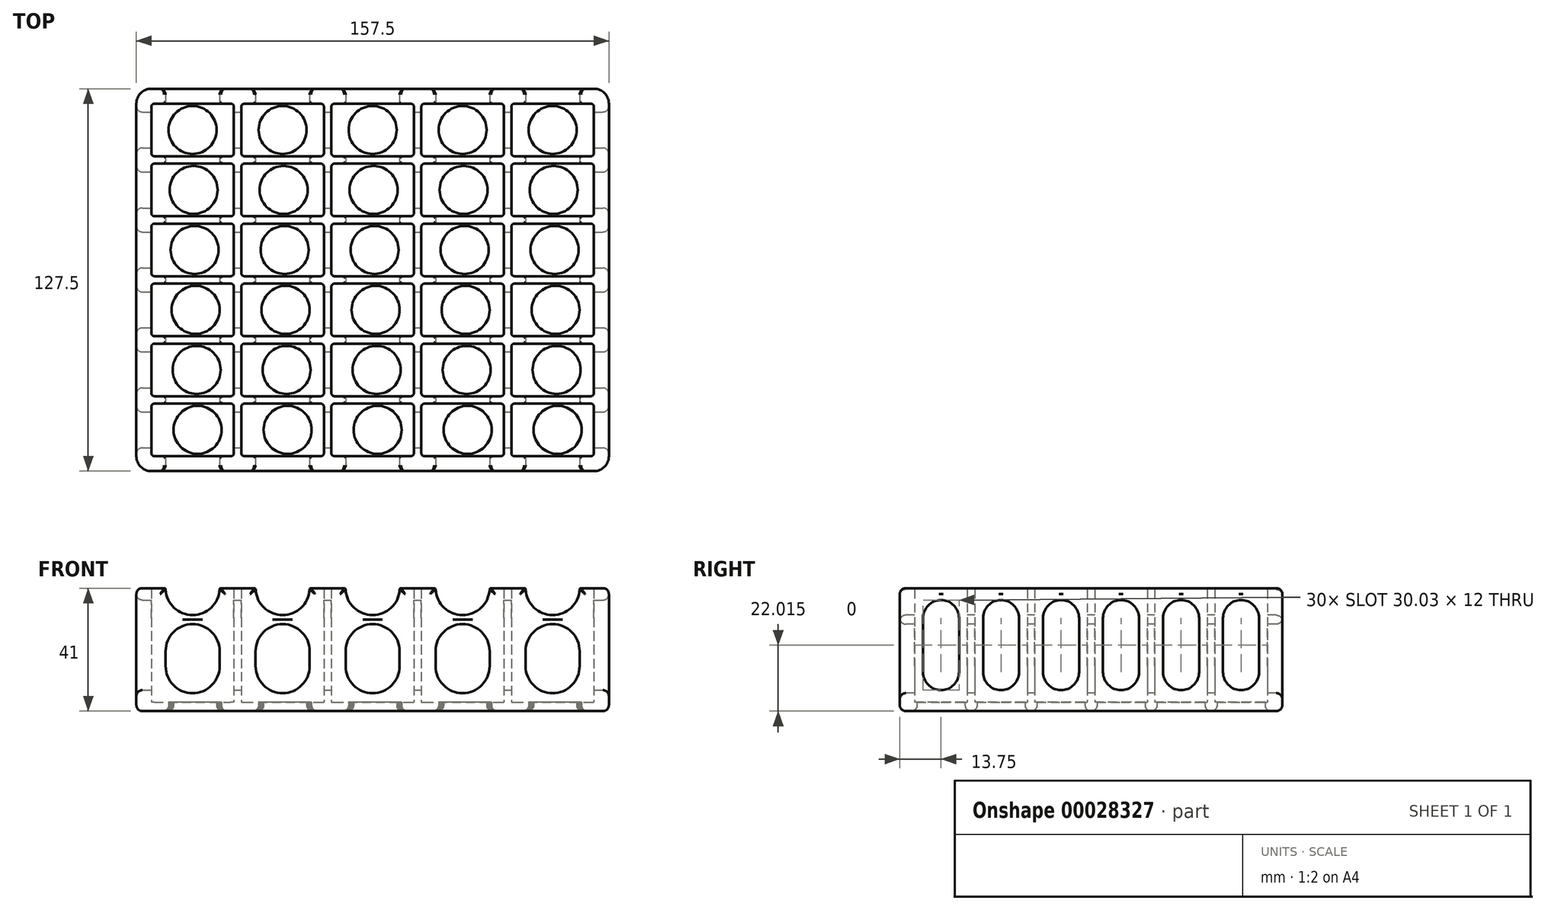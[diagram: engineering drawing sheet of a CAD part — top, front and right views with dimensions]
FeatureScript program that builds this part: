
annotation { "Feature Type Name" : "Feature", "Feature Type Description" : "" }
export const myFeature = defineFeature(function(context is Context, id is Id, definition is map)
    precondition{}
    {
        {
            var Q0;
            Q0=qCreatedBy(makeId("Top.planeOp"),FACE);
            var sketch = newSketch(context, id + "F0", { "sketchPlane" : qUnion([Q0])});
            skLineSegment(sketch, "E0.rect.bottom", {"start": v(73.75, -63.75) * mm, "end": v(-73.75, -63.75) * mm});
            skLineSegment(sketch, "E0.rect.top", {"start": v(73.75, 63.75) * mm, "end": v(-73.75, 63.75) * mm});
            skLineSegment(sketch, "E0.rect.left", {"start": v(78.75, -58.75) * mm, "end": v(78.75, 58.75) * mm});
            skLineSegment(sketch, "E0.rect.right", {"start": v(-78.75, -58.75) * mm, "end": v(-78.75, 58.75) * mm});
            skPoint(sketch, "E0.rect.middle", {"position": v(0, 0) * mm});
            skCircle(sketch, "E1", {"center": v(-60, 50) * mm, "radius": 8 * mm});
            skCircle(sketch, "E2.0.1.0", {"center": v(-59.67, 30) * mm, "radius": 8 * mm});
            skCircle(sketch, "E2.0.2.0", {"center": v(-59.33, 10) * mm, "radius": 8 * mm});
            skCircle(sketch, "E2.0.3.0", {"center": v(-59, -10) * mm, "radius": 8 * mm});
            skCircle(sketch, "E2.0.4.0", {"center": v(-58.67, -29.99) * mm, "radius": 8 * mm});
            skCircle(sketch, "E2.0.5.0", {"center": v(-58.34, -49.99) * mm, "radius": 8 * mm});
            skCircle(sketch, "E2.1.0.0", {"center": v(-30, 50) * mm, "radius": 8 * mm});
            skCircle(sketch, "E2.1.1.0", {"center": v(-29.67, 30) * mm, "radius": 8 * mm});
            skCircle(sketch, "E2.1.2.0", {"center": v(-29.33, 10) * mm, "radius": 8 * mm});
            skCircle(sketch, "E2.1.3.0", {"center": v(-29, -10) * mm, "radius": 8 * mm});
            skCircle(sketch, "E2.1.4.0", {"center": v(-28.67, -29.99) * mm, "radius": 8 * mm});
            skCircle(sketch, "E2.1.5.0", {"center": v(-28.34, -49.99) * mm, "radius": 8 * mm});
            skCircle(sketch, "E2.2.0.0", {"center": v(0, 50) * mm, "radius": 8 * mm});
            skCircle(sketch, "E2.2.1.0", {"center": v(0.33, 30) * mm, "radius": 8 * mm});
            skCircle(sketch, "E2.2.2.0", {"center": v(0.67, 10) * mm, "radius": 8 * mm});
            skCircle(sketch, "E2.2.3.0", {"center": v(1, -10) * mm, "radius": 8 * mm});
            skCircle(sketch, "E2.2.4.0", {"center": v(1.33, -29.99) * mm, "radius": 8 * mm});
            skCircle(sketch, "E2.2.5.0", {"center": v(1.66, -49.99) * mm, "radius": 8 * mm});
            skCircle(sketch, "E2.3.0.0", {"center": v(30, 50) * mm, "radius": 8 * mm});
            skCircle(sketch, "E2.3.1.0", {"center": v(30.33, 30) * mm, "radius": 8 * mm});
            skCircle(sketch, "E2.3.2.0", {"center": v(30.67, 10) * mm, "radius": 8 * mm});
            skCircle(sketch, "E2.3.3.0", {"center": v(31, -10) * mm, "radius": 8 * mm});
            skCircle(sketch, "E2.3.4.0", {"center": v(31.33, -29.99) * mm, "radius": 8 * mm});
            skCircle(sketch, "E2.3.5.0", {"center": v(31.66, -49.99) * mm, "radius": 8 * mm});
            skCircle(sketch, "E2.4.0.0", {"center": v(60, 50) * mm, "radius": 8 * mm});
            skCircle(sketch, "E2.4.1.0", {"center": v(60.33, 30) * mm, "radius": 8 * mm});
            skCircle(sketch, "E2.4.2.0", {"center": v(60.67, 10) * mm, "radius": 8 * mm});
            skCircle(sketch, "E2.4.3.0", {"center": v(61, -10) * mm, "radius": 8 * mm});
            skCircle(sketch, "E2.4.4.0", {"center": v(61.33, -29.99) * mm, "radius": 8 * mm});
            skCircle(sketch, "E2.4.5.0", {"center": v(61.66, -49.99) * mm, "radius": 8 * mm});
            skLineSegment(sketch, "E2.direction1", {"start": v(-60, 50) * mm, "end": v(-30, 50) * mm, "construction": true});
            skLineSegment(sketch, "E2.direction2", {"start": v(-60, 50) * mm, "end": v(-59.67, 30) * mm, "construction": true});
            skPoint(sketch, "E3.visualSharp", {"position": v(78.75, 63.75) * mm});
            skArc(sketch, "E3.filletArc", {"start": v(78.75, 58.75) * mm, "mid": v(77.29, 62.29) * mm, "end": v(73.75, 63.75) * mm});
            skPoint(sketch, "E4.visualSharp", {"position": v(78.75, -63.75) * mm});
            skArc(sketch, "E4.filletArc", {"start": v(73.75, -63.75) * mm, "mid": v(77.29, -62.29) * mm, "end": v(78.75, -58.75) * mm});
            skPoint(sketch, "E5.visualSharp", {"position": v(-78.75, -63.75) * mm});
            skArc(sketch, "E5.filletArc", {"start": v(-78.75, -58.75) * mm, "mid": v(-77.29, -62.29) * mm, "end": v(-73.75, -63.75) * mm});
            skPoint(sketch, "E6.visualSharp", {"position": v(-78.75, 63.75) * mm});
            skArc(sketch, "E6.filletArc", {"start": v(-73.75, 63.75) * mm, "mid": v(-77.29, 62.29) * mm, "end": v(-78.75, 58.75) * mm});
            skSolve(sketch);
        }
        {
            var Q0;
            Q0=qCreatedBy(makeId("Top.planeOp"),FACE);
            var sketch = newSketch(context, id + "F1", { "sketchPlane" : qUnion([Q0])});
            skPoint(sketch, "E7.rect.middle", {"position": v(0, 0) * mm});
            skLineSegment(sketch, "E8.bottom", {"start": v(-72.75, 58.75) * mm, "end": v(-47.25, 58.75) * mm});
            skLineSegment(sketch, "E8.top", {"start": v(-72.75, 41.25) * mm, "end": v(-47.25, 41.25) * mm});
            skLineSegment(sketch, "E8.left", {"start": v(-73.75, 57.75) * mm, "end": v(-73.75, 42.25) * mm});
            skLineSegment(sketch, "E8.right", {"start": v(-46.25, 57.75) * mm, "end": v(-46.25, 42.25) * mm});
            skPoint(sketch, "E9.visualSharp", {"position": v(-46.25, 41.25) * mm});
            skArc(sketch, "E9.filletArc", {"start": v(-47.25, 41.25) * mm, "mid": v(-46.54, 41.54) * mm, "end": v(-46.25, 42.25) * mm});
            skPoint(sketch, "E10.visualSharp", {"position": v(-46.25, 58.75) * mm});
            skArc(sketch, "E10.filletArc", {"start": v(-46.25, 57.75) * mm, "mid": v(-46.54, 58.46) * mm, "end": v(-47.25, 58.75) * mm});
            skPoint(sketch, "E11.visualSharp", {"position": v(-73.75, 58.75) * mm});
            skArc(sketch, "E11.filletArc", {"start": v(-72.75, 58.75) * mm, "mid": v(-73.46, 58.46) * mm, "end": v(-73.75, 57.75) * mm});
            skPoint(sketch, "E12.visualSharp", {"position": v(-73.75, 41.25) * mm});
            skArc(sketch, "E12.filletArc", {"start": v(-73.75, 42.25) * mm, "mid": v(-73.46, 41.54) * mm, "end": v(-72.75, 41.25) * mm});
            skLineSegment(sketch, "E13.0.1.0", {"start": v(-46.25, 37.75) * mm, "end": v(-46.25, 22.25) * mm});
            skLineSegment(sketch, "E13.0.1.1", {"start": v(-72.75, 38.75) * mm, "end": v(-47.25, 38.75) * mm});
            skPoint(sketch, "E13.0.1.2", {"position": v(-73.75, 21.25) * mm});
            skLineSegment(sketch, "E13.0.1.3", {"start": v(-72.75, 21.25) * mm, "end": v(-47.25, 21.25) * mm});
            skPoint(sketch, "E13.0.1.5", {"position": v(-46.25, 21.25) * mm});
            skLineSegment(sketch, "E13.0.1.6", {"start": v(-73.75, 37.75) * mm, "end": v(-73.75, 22.25) * mm});
            skPoint(sketch, "E13.0.1.7", {"position": v(-46.25, 38.75) * mm});
            skPoint(sketch, "E13.0.1.8", {"position": v(-73.75, 38.75) * mm});
            skPoint(sketch, "E13.0.1.10", {"position": v(-78.75, 43.75) * mm});
            skArc(sketch, "E13.0.1.11", {"start": v(-73.75, 22.25) * mm, "mid": v(-73.46, 21.54) * mm, "end": v(-72.75, 21.25) * mm});
            skArc(sketch, "E13.0.1.12", {"start": v(-47.25, 21.25) * mm, "mid": v(-46.54, 21.54) * mm, "end": v(-46.25, 22.25) * mm});
            skArc(sketch, "E13.0.1.13", {"start": v(-72.75, 38.75) * mm, "mid": v(-73.46, 38.46) * mm, "end": v(-73.75, 37.75) * mm});
            skArc(sketch, "E13.0.1.14", {"start": v(-46.25, 37.75) * mm, "mid": v(-46.54, 38.46) * mm, "end": v(-47.25, 38.75) * mm});
            skLineSegment(sketch, "E13.0.2.0", {"start": v(-46.25, 17.75) * mm, "end": v(-46.25, 2.25) * mm});
            skLineSegment(sketch, "E13.0.2.1", {"start": v(-72.75, 18.75) * mm, "end": v(-47.25, 18.75) * mm});
            skPoint(sketch, "E13.0.2.2", {"position": v(-73.75, 1.25) * mm});
            skLineSegment(sketch, "E13.0.2.3", {"start": v(-72.75, 1.25) * mm, "end": v(-47.25, 1.25) * mm});
            skLineSegment(sketch, "E13.0.2.6", {"start": v(-73.75, 17.75) * mm, "end": v(-73.75, 2.25) * mm});
            skPoint(sketch, "E13.0.2.7", {"position": v(-46.25, 18.75) * mm});
            skPoint(sketch, "E13.0.2.8", {"position": v(-73.75, 18.75) * mm});
            skPoint(sketch, "E13.0.2.10", {"position": v(-78.75, 23.75) * mm});
            skArc(sketch, "E13.0.2.11", {"start": v(-73.75, 2.25) * mm, "mid": v(-73.46, 1.54) * mm, "end": v(-72.75, 1.25) * mm});
            skArc(sketch, "E13.0.2.12", {"start": v(-47.25, 1.25) * mm, "mid": v(-46.54, 1.54) * mm, "end": v(-46.25, 2.25) * mm});
            skArc(sketch, "E13.0.2.13", {"start": v(-72.75, 18.75) * mm, "mid": v(-73.46, 18.46) * mm, "end": v(-73.75, 17.75) * mm});
            skArc(sketch, "E13.0.2.14", {"start": v(-46.25, 17.75) * mm, "mid": v(-46.54, 18.46) * mm, "end": v(-47.25, 18.75) * mm});
            skLineSegment(sketch, "E13.0.3.0", {"start": v(-46.25, -2.25) * mm, "end": v(-46.25, -17.75) * mm});
            skLineSegment(sketch, "E13.0.3.1", {"start": v(-72.75, -1.25) * mm, "end": v(-47.25, -1.25) * mm});
            skPoint(sketch, "E13.0.3.2", {"position": v(-73.75, -18.75) * mm});
            skLineSegment(sketch, "E13.0.3.3", {"start": v(-72.75, -18.75) * mm, "end": v(-47.25, -18.75) * mm});
            skPoint(sketch, "E13.0.3.5", {"position": v(-46.25, -18.75) * mm});
            skLineSegment(sketch, "E13.0.3.6", {"start": v(-73.75, -2.25) * mm, "end": v(-73.75, -17.75) * mm});
            skPoint(sketch, "E13.0.3.7", {"position": v(-46.25, -1.25) * mm});
            skPoint(sketch, "E13.0.3.8", {"position": v(-73.75, -1.25) * mm});
            skPoint(sketch, "E13.0.3.10", {"position": v(-78.75, 3.75) * mm});
            skArc(sketch, "E13.0.3.11", {"start": v(-73.75, -17.75) * mm, "mid": v(-73.46, -18.46) * mm, "end": v(-72.75, -18.75) * mm});
            skArc(sketch, "E13.0.3.12", {"start": v(-47.25, -18.75) * mm, "mid": v(-46.54, -18.46) * mm, "end": v(-46.25, -17.75) * mm});
            skArc(sketch, "E13.0.3.13", {"start": v(-72.75, -1.25) * mm, "mid": v(-73.46, -1.54) * mm, "end": v(-73.75, -2.25) * mm});
            skArc(sketch, "E13.0.3.14", {"start": v(-46.25, -2.25) * mm, "mid": v(-46.54, -1.54) * mm, "end": v(-47.25, -1.25) * mm});
            skLineSegment(sketch, "E13.0.4.0", {"start": v(-46.25, -22.25) * mm, "end": v(-46.25, -37.75) * mm});
            skLineSegment(sketch, "E13.0.4.1", {"start": v(-72.75, -21.25) * mm, "end": v(-47.25, -21.25) * mm});
            skPoint(sketch, "E13.0.4.2", {"position": v(-73.75, -38.75) * mm});
            skLineSegment(sketch, "E13.0.4.3", {"start": v(-72.75, -38.75) * mm, "end": v(-47.25, -38.75) * mm});
            skPoint(sketch, "E13.0.4.5", {"position": v(-46.25, -38.75) * mm});
            skLineSegment(sketch, "E13.0.4.6", {"start": v(-73.75, -22.25) * mm, "end": v(-73.75, -37.75) * mm});
            skPoint(sketch, "E13.0.4.7", {"position": v(-46.25, -21.25) * mm});
            skPoint(sketch, "E13.0.4.8", {"position": v(-73.75, -21.25) * mm});
            skPoint(sketch, "E13.0.4.10", {"position": v(-78.75, -16.25) * mm});
            skArc(sketch, "E13.0.4.11", {"start": v(-73.75, -37.75) * mm, "mid": v(-73.46, -38.46) * mm, "end": v(-72.75, -38.75) * mm});
            skArc(sketch, "E13.0.4.12", {"start": v(-47.25, -38.75) * mm, "mid": v(-46.54, -38.46) * mm, "end": v(-46.25, -37.75) * mm});
            skArc(sketch, "E13.0.4.13", {"start": v(-72.75, -21.25) * mm, "mid": v(-73.46, -21.54) * mm, "end": v(-73.75, -22.25) * mm});
            skArc(sketch, "E13.0.4.14", {"start": v(-46.25, -22.25) * mm, "mid": v(-46.54, -21.54) * mm, "end": v(-47.25, -21.25) * mm});
            skLineSegment(sketch, "E13.0.5.0", {"start": v(-46.25, -42.25) * mm, "end": v(-46.25, -57.75) * mm});
            skLineSegment(sketch, "E13.0.5.1", {"start": v(-72.75, -41.25) * mm, "end": v(-47.25, -41.25) * mm});
            skPoint(sketch, "E13.0.5.2", {"position": v(-73.75, -58.75) * mm});
            skLineSegment(sketch, "E13.0.5.3", {"start": v(-72.75, -58.75) * mm, "end": v(-47.25, -58.75) * mm});
            skPoint(sketch, "E13.0.5.5", {"position": v(-46.25, -58.75) * mm});
            skLineSegment(sketch, "E13.0.5.6", {"start": v(-73.75, -42.25) * mm, "end": v(-73.75, -57.75) * mm});
            skPoint(sketch, "E13.0.5.7", {"position": v(-46.25, -41.25) * mm});
            skPoint(sketch, "E13.0.5.8", {"position": v(-73.75, -41.25) * mm});
            skPoint(sketch, "E13.0.5.10", {"position": v(-78.75, -36.25) * mm});
            skArc(sketch, "E13.0.5.11", {"start": v(-73.75, -57.75) * mm, "mid": v(-73.46, -58.46) * mm, "end": v(-72.75, -58.75) * mm});
            skArc(sketch, "E13.0.5.12", {"start": v(-47.25, -58.75) * mm, "mid": v(-46.54, -58.46) * mm, "end": v(-46.25, -57.75) * mm});
            skArc(sketch, "E13.0.5.13", {"start": v(-72.75, -41.25) * mm, "mid": v(-73.46, -41.54) * mm, "end": v(-73.75, -42.25) * mm});
            skArc(sketch, "E13.0.5.14", {"start": v(-46.25, -42.25) * mm, "mid": v(-46.54, -41.54) * mm, "end": v(-47.25, -41.25) * mm});
            skLineSegment(sketch, "E13.1.0.0", {"start": v(-16.25, 57.75) * mm, "end": v(-16.25, 42.25) * mm});
            skLineSegment(sketch, "E13.1.0.1", {"start": v(-42.75, 58.75) * mm, "end": v(-17.25, 58.75) * mm});
            skPoint(sketch, "E13.1.0.2", {"position": v(-43.75, 41.25) * mm});
            skLineSegment(sketch, "E13.1.0.3", {"start": v(-42.75, 41.25) * mm, "end": v(-17.25, 41.25) * mm});
            skPoint(sketch, "E13.1.0.5", {"position": v(-16.25, 41.25) * mm});
            skLineSegment(sketch, "E13.1.0.6", {"start": v(-43.75, 57.75) * mm, "end": v(-43.75, 42.25) * mm});
            skPoint(sketch, "E13.1.0.7", {"position": v(-16.25, 58.75) * mm});
            skPoint(sketch, "E13.1.0.8", {"position": v(-43.75, 58.75) * mm});
            skPoint(sketch, "E13.1.0.10", {"position": v(-48.75, 63.75) * mm});
            skArc(sketch, "E13.1.0.11", {"start": v(-43.75, 42.25) * mm, "mid": v(-43.46, 41.54) * mm, "end": v(-42.75, 41.25) * mm});
            skArc(sketch, "E13.1.0.12", {"start": v(-17.25, 41.25) * mm, "mid": v(-16.54, 41.54) * mm, "end": v(-16.25, 42.25) * mm});
            skArc(sketch, "E13.1.0.13", {"start": v(-42.75, 58.75) * mm, "mid": v(-43.46, 58.46) * mm, "end": v(-43.75, 57.75) * mm});
            skArc(sketch, "E13.1.0.14", {"start": v(-16.25, 57.75) * mm, "mid": v(-16.54, 58.46) * mm, "end": v(-17.25, 58.75) * mm});
            skLineSegment(sketch, "E13.1.1.0", {"start": v(-16.25, 37.75) * mm, "end": v(-16.25, 22.25) * mm});
            skLineSegment(sketch, "E13.1.1.1", {"start": v(-42.75, 38.75) * mm, "end": v(-17.25, 38.75) * mm});
            skPoint(sketch, "E13.1.1.2", {"position": v(-43.75, 21.25) * mm});
            skLineSegment(sketch, "E13.1.1.3", {"start": v(-42.75, 21.25) * mm, "end": v(-17.25, 21.25) * mm});
            skPoint(sketch, "E13.1.1.5", {"position": v(-16.25, 21.25) * mm});
            skLineSegment(sketch, "E13.1.1.6", {"start": v(-43.75, 37.75) * mm, "end": v(-43.75, 22.25) * mm});
            skPoint(sketch, "E13.1.1.7", {"position": v(-16.25, 38.75) * mm});
            skPoint(sketch, "E13.1.1.8", {"position": v(-43.75, 38.75) * mm});
            skPoint(sketch, "E13.1.1.10", {"position": v(-48.75, 43.75) * mm});
            skArc(sketch, "E13.1.1.11", {"start": v(-43.75, 22.25) * mm, "mid": v(-43.46, 21.54) * mm, "end": v(-42.75, 21.25) * mm});
            skArc(sketch, "E13.1.1.12", {"start": v(-17.25, 21.25) * mm, "mid": v(-16.54, 21.54) * mm, "end": v(-16.25, 22.25) * mm});
            skArc(sketch, "E13.1.1.13", {"start": v(-42.75, 38.75) * mm, "mid": v(-43.46, 38.46) * mm, "end": v(-43.75, 37.75) * mm});
            skArc(sketch, "E13.1.1.14", {"start": v(-16.25, 37.75) * mm, "mid": v(-16.54, 38.46) * mm, "end": v(-17.25, 38.75) * mm});
            skLineSegment(sketch, "E13.1.2.0", {"start": v(-16.25, 17.75) * mm, "end": v(-16.25, 2.25) * mm});
            skLineSegment(sketch, "E13.1.2.1", {"start": v(-42.75, 18.75) * mm, "end": v(-17.25, 18.75) * mm});
            skLineSegment(sketch, "E13.1.2.3", {"start": v(-42.75, 1.25) * mm, "end": v(-17.25, 1.25) * mm});
            skPoint(sketch, "E13.1.2.5", {"position": v(-16.25, 1.25) * mm});
            skLineSegment(sketch, "E13.1.2.6", {"start": v(-43.75, 17.75) * mm, "end": v(-43.75, 2.25) * mm});
            skPoint(sketch, "E13.1.2.7", {"position": v(-16.25, 18.75) * mm});
            skPoint(sketch, "E13.1.2.8", {"position": v(-43.75, 18.75) * mm});
            skPoint(sketch, "E13.1.2.10", {"position": v(-48.75, 23.75) * mm});
            skArc(sketch, "E13.1.2.11", {"start": v(-43.75, 2.25) * mm, "mid": v(-43.46, 1.54) * mm, "end": v(-42.75, 1.25) * mm});
            skArc(sketch, "E13.1.2.12", {"start": v(-17.25, 1.25) * mm, "mid": v(-16.54, 1.54) * mm, "end": v(-16.25, 2.25) * mm});
            skArc(sketch, "E13.1.2.13", {"start": v(-42.75, 18.75) * mm, "mid": v(-43.46, 18.46) * mm, "end": v(-43.75, 17.75) * mm});
            skArc(sketch, "E13.1.2.14", {"start": v(-16.25, 17.75) * mm, "mid": v(-16.54, 18.46) * mm, "end": v(-17.25, 18.75) * mm});
            skLineSegment(sketch, "E13.1.3.0", {"start": v(-16.25, -2.25) * mm, "end": v(-16.25, -17.75) * mm});
            skLineSegment(sketch, "E13.1.3.1", {"start": v(-42.75, -1.25) * mm, "end": v(-17.25, -1.25) * mm});
            skPoint(sketch, "E13.1.3.2", {"position": v(-43.75, -18.75) * mm});
            skLineSegment(sketch, "E13.1.3.3", {"start": v(-42.75, -18.75) * mm, "end": v(-17.25, -18.75) * mm});
            skPoint(sketch, "E13.1.3.5", {"position": v(-16.25, -18.75) * mm});
            skLineSegment(sketch, "E13.1.3.6", {"start": v(-43.75, -2.25) * mm, "end": v(-43.75, -17.75) * mm});
            skPoint(sketch, "E13.1.3.7", {"position": v(-16.25, -1.25) * mm});
            skPoint(sketch, "E13.1.3.8", {"position": v(-43.75, -1.25) * mm});
            skPoint(sketch, "E13.1.3.10", {"position": v(-48.75, 3.75) * mm});
            skArc(sketch, "E13.1.3.11", {"start": v(-43.75, -17.75) * mm, "mid": v(-43.46, -18.46) * mm, "end": v(-42.75, -18.75) * mm});
            skArc(sketch, "E13.1.3.12", {"start": v(-17.25, -18.75) * mm, "mid": v(-16.54, -18.46) * mm, "end": v(-16.25, -17.75) * mm});
            skArc(sketch, "E13.1.3.13", {"start": v(-42.75, -1.25) * mm, "mid": v(-43.46, -1.54) * mm, "end": v(-43.75, -2.25) * mm});
            skArc(sketch, "E13.1.3.14", {"start": v(-16.25, -2.25) * mm, "mid": v(-16.54, -1.54) * mm, "end": v(-17.25, -1.25) * mm});
            skLineSegment(sketch, "E13.1.4.0", {"start": v(-16.25, -22.25) * mm, "end": v(-16.25, -37.75) * mm});
            skLineSegment(sketch, "E13.1.4.1", {"start": v(-42.75, -21.25) * mm, "end": v(-17.25, -21.25) * mm});
            skPoint(sketch, "E13.1.4.2", {"position": v(-43.75, -38.75) * mm});
            skLineSegment(sketch, "E13.1.4.3", {"start": v(-42.75, -38.75) * mm, "end": v(-17.25, -38.75) * mm});
            skPoint(sketch, "E13.1.4.5", {"position": v(-16.25, -38.75) * mm});
            skLineSegment(sketch, "E13.1.4.6", {"start": v(-43.75, -22.25) * mm, "end": v(-43.75, -37.75) * mm});
            skPoint(sketch, "E13.1.4.7", {"position": v(-16.25, -21.25) * mm});
            skPoint(sketch, "E13.1.4.8", {"position": v(-43.75, -21.25) * mm});
            skPoint(sketch, "E13.1.4.10", {"position": v(-48.75, -16.25) * mm});
            skArc(sketch, "E13.1.4.11", {"start": v(-43.75, -37.75) * mm, "mid": v(-43.46, -38.46) * mm, "end": v(-42.75, -38.75) * mm});
            skArc(sketch, "E13.1.4.12", {"start": v(-17.25, -38.75) * mm, "mid": v(-16.54, -38.46) * mm, "end": v(-16.25, -37.75) * mm});
            skArc(sketch, "E13.1.4.13", {"start": v(-42.75, -21.25) * mm, "mid": v(-43.46, -21.54) * mm, "end": v(-43.75, -22.25) * mm});
            skArc(sketch, "E13.1.4.14", {"start": v(-16.25, -22.25) * mm, "mid": v(-16.54, -21.54) * mm, "end": v(-17.25, -21.25) * mm});
            skLineSegment(sketch, "E13.1.5.0", {"start": v(-16.25, -42.25) * mm, "end": v(-16.25, -57.75) * mm});
            skLineSegment(sketch, "E13.1.5.1", {"start": v(-42.75, -41.25) * mm, "end": v(-17.25, -41.25) * mm});
            skLineSegment(sketch, "E13.1.5.3", {"start": v(-42.75, -58.75) * mm, "end": v(-17.25, -58.75) * mm});
            skPoint(sketch, "E13.1.5.5", {"position": v(-16.25, -58.75) * mm});
            skLineSegment(sketch, "E13.1.5.6", {"start": v(-43.75, -42.25) * mm, "end": v(-43.75, -57.75) * mm});
            skPoint(sketch, "E13.1.5.7", {"position": v(-16.25, -41.25) * mm});
            skPoint(sketch, "E13.1.5.8", {"position": v(-43.75, -41.25) * mm});
            skPoint(sketch, "E13.1.5.10", {"position": v(-48.75, -36.25) * mm});
            skArc(sketch, "E13.1.5.11", {"start": v(-43.75, -57.75) * mm, "mid": v(-43.46, -58.46) * mm, "end": v(-42.75, -58.75) * mm});
            skArc(sketch, "E13.1.5.12", {"start": v(-17.25, -58.75) * mm, "mid": v(-16.54, -58.46) * mm, "end": v(-16.25, -57.75) * mm});
            skArc(sketch, "E13.1.5.13", {"start": v(-42.75, -41.25) * mm, "mid": v(-43.46, -41.54) * mm, "end": v(-43.75, -42.25) * mm});
            skArc(sketch, "E13.1.5.14", {"start": v(-16.25, -42.25) * mm, "mid": v(-16.54, -41.54) * mm, "end": v(-17.25, -41.25) * mm});
            skLineSegment(sketch, "E13.2.0.0", {"start": v(13.75, 57.75) * mm, "end": v(13.75, 42.25) * mm});
            skLineSegment(sketch, "E13.2.0.1", {"start": v(-12.75, 58.75) * mm, "end": v(12.75, 58.75) * mm});
            skLineSegment(sketch, "E13.2.0.3", {"start": v(-12.75, 41.25) * mm, "end": v(12.75, 41.25) * mm});
            skPoint(sketch, "E13.2.0.5", {"position": v(13.75, 41.25) * mm});
            skLineSegment(sketch, "E13.2.0.6", {"start": v(-13.75, 57.75) * mm, "end": v(-13.75, 42.25) * mm});
            skPoint(sketch, "E13.2.0.7", {"position": v(13.75, 58.75) * mm});
            skPoint(sketch, "E13.2.0.8", {"position": v(-13.75, 58.75) * mm});
            skPoint(sketch, "E13.2.0.10", {"position": v(-18.75, 63.75) * mm});
            skArc(sketch, "E13.2.0.11", {"start": v(-13.75, 42.25) * mm, "mid": v(-13.46, 41.54) * mm, "end": v(-12.75, 41.25) * mm});
            skArc(sketch, "E13.2.0.12", {"start": v(12.75, 41.25) * mm, "mid": v(13.46, 41.54) * mm, "end": v(13.75, 42.25) * mm});
            skArc(sketch, "E13.2.0.13", {"start": v(-12.75, 58.75) * mm, "mid": v(-13.46, 58.46) * mm, "end": v(-13.75, 57.75) * mm});
            skArc(sketch, "E13.2.0.14", {"start": v(13.75, 57.75) * mm, "mid": v(13.46, 58.46) * mm, "end": v(12.75, 58.75) * mm});
            skLineSegment(sketch, "E13.2.1.0", {"start": v(13.75, 37.75) * mm, "end": v(13.75, 22.25) * mm});
            skLineSegment(sketch, "E13.2.1.1", {"start": v(-12.75, 38.75) * mm, "end": v(12.75, 38.75) * mm});
            skPoint(sketch, "E13.2.1.2", {"position": v(-13.75, 21.25) * mm});
            skLineSegment(sketch, "E13.2.1.3", {"start": v(-12.75, 21.25) * mm, "end": v(12.75, 21.25) * mm});
            skPoint(sketch, "E13.2.1.5", {"position": v(13.75, 21.25) * mm});
            skLineSegment(sketch, "E13.2.1.6", {"start": v(-13.75, 37.75) * mm, "end": v(-13.75, 22.25) * mm});
            skPoint(sketch, "E13.2.1.7", {"position": v(13.75, 38.75) * mm});
            skPoint(sketch, "E13.2.1.8", {"position": v(-13.75, 38.75) * mm});
            skPoint(sketch, "E13.2.1.10", {"position": v(-18.75, 43.75) * mm});
            skArc(sketch, "E13.2.1.11", {"start": v(-13.75, 22.25) * mm, "mid": v(-13.46, 21.54) * mm, "end": v(-12.75, 21.25) * mm});
            skArc(sketch, "E13.2.1.12", {"start": v(12.75, 21.25) * mm, "mid": v(13.46, 21.54) * mm, "end": v(13.75, 22.25) * mm});
            skArc(sketch, "E13.2.1.13", {"start": v(-12.75, 38.75) * mm, "mid": v(-13.46, 38.46) * mm, "end": v(-13.75, 37.75) * mm});
            skArc(sketch, "E13.2.1.14", {"start": v(13.75, 37.75) * mm, "mid": v(13.46, 38.46) * mm, "end": v(12.75, 38.75) * mm});
            skLineSegment(sketch, "E13.2.2.0", {"start": v(13.75, 17.75) * mm, "end": v(13.75, 2.25) * mm});
            skLineSegment(sketch, "E13.2.2.1", {"start": v(-12.75, 18.75) * mm, "end": v(12.75, 18.75) * mm});
            skPoint(sketch, "E13.2.2.2", {"position": v(-13.75, 1.25) * mm});
            skLineSegment(sketch, "E13.2.2.3", {"start": v(-12.75, 1.25) * mm, "end": v(12.75, 1.25) * mm});
            skPoint(sketch, "E13.2.2.5", {"position": v(13.75, 1.25) * mm});
            skLineSegment(sketch, "E13.2.2.6", {"start": v(-13.75, 17.75) * mm, "end": v(-13.75, 2.25) * mm});
            skPoint(sketch, "E13.2.2.7", {"position": v(13.75, 18.75) * mm});
            skPoint(sketch, "E13.2.2.8", {"position": v(-13.75, 18.75) * mm});
            skPoint(sketch, "E13.2.2.10", {"position": v(-18.75, 23.75) * mm});
            skArc(sketch, "E13.2.2.11", {"start": v(-13.75, 2.25) * mm, "mid": v(-13.46, 1.54) * mm, "end": v(-12.75, 1.25) * mm});
            skArc(sketch, "E13.2.2.12", {"start": v(12.75, 1.25) * mm, "mid": v(13.46, 1.54) * mm, "end": v(13.75, 2.25) * mm});
            skArc(sketch, "E13.2.2.13", {"start": v(-12.75, 18.75) * mm, "mid": v(-13.46, 18.46) * mm, "end": v(-13.75, 17.75) * mm});
            skArc(sketch, "E13.2.2.14", {"start": v(13.75, 17.75) * mm, "mid": v(13.46, 18.46) * mm, "end": v(12.75, 18.75) * mm});
            skLineSegment(sketch, "E13.2.3.0", {"start": v(13.75, -2.25) * mm, "end": v(13.75, -17.75) * mm});
            skLineSegment(sketch, "E13.2.3.1", {"start": v(-12.75, -1.25) * mm, "end": v(12.75, -1.25) * mm});
            skPoint(sketch, "E13.2.3.2", {"position": v(-13.75, -18.75) * mm});
            skLineSegment(sketch, "E13.2.3.3", {"start": v(-12.75, -18.75) * mm, "end": v(12.75, -18.75) * mm});
            skPoint(sketch, "E13.2.3.5", {"position": v(13.75, -18.75) * mm});
            skLineSegment(sketch, "E13.2.3.6", {"start": v(-13.75, -2.25) * mm, "end": v(-13.75, -17.75) * mm});
            skPoint(sketch, "E13.2.3.7", {"position": v(13.75, -1.25) * mm});
            skPoint(sketch, "E13.2.3.8", {"position": v(-13.75, -1.25) * mm});
            skPoint(sketch, "E13.2.3.10", {"position": v(-18.75, 3.75) * mm});
            skArc(sketch, "E13.2.3.11", {"start": v(-13.75, -17.75) * mm, "mid": v(-13.46, -18.46) * mm, "end": v(-12.75, -18.75) * mm});
            skArc(sketch, "E13.2.3.12", {"start": v(12.75, -18.75) * mm, "mid": v(13.46, -18.46) * mm, "end": v(13.75, -17.75) * mm});
            skArc(sketch, "E13.2.3.13", {"start": v(-12.75, -1.25) * mm, "mid": v(-13.46, -1.54) * mm, "end": v(-13.75, -2.25) * mm});
            skArc(sketch, "E13.2.3.14", {"start": v(13.75, -2.25) * mm, "mid": v(13.46, -1.54) * mm, "end": v(12.75, -1.25) * mm});
            skLineSegment(sketch, "E13.2.4.0", {"start": v(13.75, -22.25) * mm, "end": v(13.75, -37.75) * mm});
            skLineSegment(sketch, "E13.2.4.1", {"start": v(-12.75, -21.25) * mm, "end": v(12.75, -21.25) * mm});
            skPoint(sketch, "E13.2.4.2", {"position": v(-13.75, -38.75) * mm});
            skLineSegment(sketch, "E13.2.4.3", {"start": v(-12.75, -38.75) * mm, "end": v(12.75, -38.75) * mm});
            skPoint(sketch, "E13.2.4.5", {"position": v(13.75, -38.75) * mm});
            skLineSegment(sketch, "E13.2.4.6", {"start": v(-13.75, -22.25) * mm, "end": v(-13.75, -37.75) * mm});
            skPoint(sketch, "E13.2.4.7", {"position": v(13.75, -21.25) * mm});
            skPoint(sketch, "E13.2.4.8", {"position": v(-13.75, -21.25) * mm});
            skPoint(sketch, "E13.2.4.10", {"position": v(-18.75, -16.25) * mm});
            skArc(sketch, "E13.2.4.11", {"start": v(-13.75, -37.75) * mm, "mid": v(-13.46, -38.46) * mm, "end": v(-12.75, -38.75) * mm});
            skArc(sketch, "E13.2.4.12", {"start": v(12.75, -38.75) * mm, "mid": v(13.46, -38.46) * mm, "end": v(13.75, -37.75) * mm});
            skArc(sketch, "E13.2.4.13", {"start": v(-12.75, -21.25) * mm, "mid": v(-13.46, -21.54) * mm, "end": v(-13.75, -22.25) * mm});
            skArc(sketch, "E13.2.4.14", {"start": v(13.75, -22.25) * mm, "mid": v(13.46, -21.54) * mm, "end": v(12.75, -21.25) * mm});
            skLineSegment(sketch, "E13.2.5.0", {"start": v(13.75, -42.25) * mm, "end": v(13.75, -57.75) * mm});
            skLineSegment(sketch, "E13.2.5.1", {"start": v(-12.75, -41.25) * mm, "end": v(12.75, -41.25) * mm});
            skLineSegment(sketch, "E13.2.5.3", {"start": v(-12.75, -58.75) * mm, "end": v(12.75, -58.75) * mm});
            skPoint(sketch, "E13.2.5.5", {"position": v(13.75, -58.75) * mm});
            skLineSegment(sketch, "E13.2.5.6", {"start": v(-13.75, -42.25) * mm, "end": v(-13.75, -57.75) * mm});
            skPoint(sketch, "E13.2.5.7", {"position": v(13.75, -41.25) * mm});
            skPoint(sketch, "E13.2.5.8", {"position": v(-13.75, -41.25) * mm});
            skPoint(sketch, "E13.2.5.10", {"position": v(-18.75, -36.25) * mm});
            skArc(sketch, "E13.2.5.11", {"start": v(-13.75, -57.75) * mm, "mid": v(-13.46, -58.46) * mm, "end": v(-12.75, -58.75) * mm});
            skArc(sketch, "E13.2.5.12", {"start": v(12.75, -58.75) * mm, "mid": v(13.46, -58.46) * mm, "end": v(13.75, -57.75) * mm});
            skArc(sketch, "E13.2.5.13", {"start": v(-12.75, -41.25) * mm, "mid": v(-13.46, -41.54) * mm, "end": v(-13.75, -42.25) * mm});
            skArc(sketch, "E13.2.5.14", {"start": v(13.75, -42.25) * mm, "mid": v(13.46, -41.54) * mm, "end": v(12.75, -41.25) * mm});
            skLineSegment(sketch, "E13.3.0.0", {"start": v(43.75, 57.75) * mm, "end": v(43.75, 42.25) * mm});
            skLineSegment(sketch, "E13.3.0.1", {"start": v(17.25, 58.75) * mm, "end": v(42.75, 58.75) * mm});
            skPoint(sketch, "E13.3.0.2", {"position": v(16.25, 41.25) * mm});
            skLineSegment(sketch, "E13.3.0.3", {"start": v(17.25, 41.25) * mm, "end": v(42.75, 41.25) * mm});
            skPoint(sketch, "E13.3.0.5", {"position": v(43.75, 41.25) * mm});
            skLineSegment(sketch, "E13.3.0.6", {"start": v(16.25, 57.75) * mm, "end": v(16.25, 42.25) * mm});
            skPoint(sketch, "E13.3.0.7", {"position": v(43.75, 58.75) * mm});
            skPoint(sketch, "E13.3.0.8", {"position": v(16.25, 58.75) * mm});
            skPoint(sketch, "E13.3.0.10", {"position": v(11.25, 63.75) * mm});
            skArc(sketch, "E13.3.0.11", {"start": v(16.25, 42.25) * mm, "mid": v(16.54, 41.54) * mm, "end": v(17.25, 41.25) * mm});
            skArc(sketch, "E13.3.0.12", {"start": v(42.75, 41.25) * mm, "mid": v(43.46, 41.54) * mm, "end": v(43.75, 42.25) * mm});
            skArc(sketch, "E13.3.0.13", {"start": v(17.25, 58.75) * mm, "mid": v(16.54, 58.46) * mm, "end": v(16.25, 57.75) * mm});
            skArc(sketch, "E13.3.0.14", {"start": v(43.75, 57.75) * mm, "mid": v(43.46, 58.46) * mm, "end": v(42.75, 58.75) * mm});
            skLineSegment(sketch, "E13.3.1.0", {"start": v(43.75, 37.75) * mm, "end": v(43.75, 22.25) * mm});
            skLineSegment(sketch, "E13.3.1.1", {"start": v(17.25, 38.75) * mm, "end": v(42.75, 38.75) * mm});
            skPoint(sketch, "E13.3.1.2", {"position": v(16.25, 21.25) * mm});
            skLineSegment(sketch, "E13.3.1.3", {"start": v(17.25, 21.25) * mm, "end": v(42.75, 21.25) * mm});
            skPoint(sketch, "E13.3.1.5", {"position": v(43.75, 21.25) * mm});
            skLineSegment(sketch, "E13.3.1.6", {"start": v(16.25, 37.75) * mm, "end": v(16.25, 22.25) * mm});
            skPoint(sketch, "E13.3.1.7", {"position": v(43.75, 38.75) * mm});
            skPoint(sketch, "E13.3.1.8", {"position": v(16.25, 38.75) * mm});
            skPoint(sketch, "E13.3.1.10", {"position": v(11.25, 43.75) * mm});
            skArc(sketch, "E13.3.1.11", {"start": v(16.25, 22.25) * mm, "mid": v(16.54, 21.54) * mm, "end": v(17.25, 21.25) * mm});
            skArc(sketch, "E13.3.1.12", {"start": v(42.75, 21.25) * mm, "mid": v(43.46, 21.54) * mm, "end": v(43.75, 22.25) * mm});
            skArc(sketch, "E13.3.1.13", {"start": v(17.25, 38.75) * mm, "mid": v(16.54, 38.46) * mm, "end": v(16.25, 37.75) * mm});
            skArc(sketch, "E13.3.1.14", {"start": v(43.75, 37.75) * mm, "mid": v(43.46, 38.46) * mm, "end": v(42.75, 38.75) * mm});
            skLineSegment(sketch, "E13.3.2.0", {"start": v(43.75, 17.75) * mm, "end": v(43.75, 2.25) * mm});
            skLineSegment(sketch, "E13.3.2.1", {"start": v(17.25, 18.75) * mm, "end": v(42.75, 18.75) * mm});
            skPoint(sketch, "E13.3.2.2", {"position": v(16.25, 1.25) * mm});
            skLineSegment(sketch, "E13.3.2.3", {"start": v(17.25, 1.25) * mm, "end": v(42.75, 1.25) * mm});
            skPoint(sketch, "E13.3.2.5", {"position": v(43.75, 1.25) * mm});
            skLineSegment(sketch, "E13.3.2.6", {"start": v(16.25, 17.75) * mm, "end": v(16.25, 2.25) * mm});
            skPoint(sketch, "E13.3.2.7", {"position": v(43.75, 18.75) * mm});
            skPoint(sketch, "E13.3.2.8", {"position": v(16.25, 18.75) * mm});
            skPoint(sketch, "E13.3.2.10", {"position": v(11.25, 23.75) * mm});
            skArc(sketch, "E13.3.2.11", {"start": v(16.25, 2.25) * mm, "mid": v(16.54, 1.54) * mm, "end": v(17.25, 1.25) * mm});
            skArc(sketch, "E13.3.2.12", {"start": v(42.75, 1.25) * mm, "mid": v(43.46, 1.54) * mm, "end": v(43.75, 2.25) * mm});
            skArc(sketch, "E13.3.2.13", {"start": v(17.25, 18.75) * mm, "mid": v(16.54, 18.46) * mm, "end": v(16.25, 17.75) * mm});
            skArc(sketch, "E13.3.2.14", {"start": v(43.75, 17.75) * mm, "mid": v(43.46, 18.46) * mm, "end": v(42.75, 18.75) * mm});
            skLineSegment(sketch, "E13.3.3.0", {"start": v(43.75, -2.25) * mm, "end": v(43.75, -17.75) * mm});
            skLineSegment(sketch, "E13.3.3.1", {"start": v(17.25, -1.25) * mm, "end": v(42.75, -1.25) * mm});
            skPoint(sketch, "E13.3.3.2", {"position": v(16.25, -18.75) * mm});
            skLineSegment(sketch, "E13.3.3.3", {"start": v(17.25, -18.75) * mm, "end": v(42.75, -18.75) * mm});
            skLineSegment(sketch, "E13.3.3.6", {"start": v(16.25, -2.25) * mm, "end": v(16.25, -17.75) * mm});
            skPoint(sketch, "E13.3.3.7", {"position": v(43.75, -1.25) * mm});
            skPoint(sketch, "E13.3.3.8", {"position": v(16.25, -1.25) * mm});
            skPoint(sketch, "E13.3.3.10", {"position": v(11.25, 3.75) * mm});
            skArc(sketch, "E13.3.3.11", {"start": v(16.25, -17.75) * mm, "mid": v(16.54, -18.46) * mm, "end": v(17.25, -18.75) * mm});
            skArc(sketch, "E13.3.3.12", {"start": v(42.75, -18.75) * mm, "mid": v(43.46, -18.46) * mm, "end": v(43.75, -17.75) * mm});
            skArc(sketch, "E13.3.3.13", {"start": v(17.25, -1.25) * mm, "mid": v(16.54, -1.54) * mm, "end": v(16.25, -2.25) * mm});
            skArc(sketch, "E13.3.3.14", {"start": v(43.75, -2.25) * mm, "mid": v(43.46, -1.54) * mm, "end": v(42.75, -1.25) * mm});
            skLineSegment(sketch, "E13.3.4.0", {"start": v(43.75, -22.25) * mm, "end": v(43.75, -37.75) * mm});
            skLineSegment(sketch, "E13.3.4.1", {"start": v(17.25, -21.25) * mm, "end": v(42.75, -21.25) * mm});
            skPoint(sketch, "E13.3.4.2", {"position": v(16.25, -38.75) * mm});
            skLineSegment(sketch, "E13.3.4.3", {"start": v(17.25, -38.75) * mm, "end": v(42.75, -38.75) * mm});
            skPoint(sketch, "E13.3.4.5", {"position": v(43.75, -38.75) * mm});
            skLineSegment(sketch, "E13.3.4.6", {"start": v(16.25, -22.25) * mm, "end": v(16.25, -37.75) * mm});
            skPoint(sketch, "E13.3.4.7", {"position": v(43.75, -21.25) * mm});
            skPoint(sketch, "E13.3.4.8", {"position": v(16.25, -21.25) * mm});
            skPoint(sketch, "E13.3.4.10", {"position": v(11.25, -16.25) * mm});
            skArc(sketch, "E13.3.4.11", {"start": v(16.25, -37.75) * mm, "mid": v(16.54, -38.46) * mm, "end": v(17.25, -38.75) * mm});
            skArc(sketch, "E13.3.4.12", {"start": v(42.75, -38.75) * mm, "mid": v(43.46, -38.46) * mm, "end": v(43.75, -37.75) * mm});
            skArc(sketch, "E13.3.4.13", {"start": v(17.25, -21.25) * mm, "mid": v(16.54, -21.54) * mm, "end": v(16.25, -22.25) * mm});
            skArc(sketch, "E13.3.4.14", {"start": v(43.75, -22.25) * mm, "mid": v(43.46, -21.54) * mm, "end": v(42.75, -21.25) * mm});
            skLineSegment(sketch, "E13.3.5.0", {"start": v(43.75, -42.25) * mm, "end": v(43.75, -57.75) * mm});
            skLineSegment(sketch, "E13.3.5.1", {"start": v(17.25, -41.25) * mm, "end": v(42.75, -41.25) * mm});
            skLineSegment(sketch, "E13.3.5.3", {"start": v(17.25, -58.75) * mm, "end": v(42.75, -58.75) * mm});
            skPoint(sketch, "E13.3.5.5", {"position": v(43.75, -58.75) * mm});
            skLineSegment(sketch, "E13.3.5.6", {"start": v(16.25, -42.25) * mm, "end": v(16.25, -57.75) * mm});
            skPoint(sketch, "E13.3.5.7", {"position": v(43.75, -41.25) * mm});
            skPoint(sketch, "E13.3.5.8", {"position": v(16.25, -41.25) * mm});
            skPoint(sketch, "E13.3.5.10", {"position": v(11.25, -36.25) * mm});
            skArc(sketch, "E13.3.5.11", {"start": v(16.25, -57.75) * mm, "mid": v(16.54, -58.46) * mm, "end": v(17.25, -58.75) * mm});
            skArc(sketch, "E13.3.5.12", {"start": v(42.75, -58.75) * mm, "mid": v(43.46, -58.46) * mm, "end": v(43.75, -57.75) * mm});
            skArc(sketch, "E13.3.5.13", {"start": v(17.25, -41.25) * mm, "mid": v(16.54, -41.54) * mm, "end": v(16.25, -42.25) * mm});
            skArc(sketch, "E13.3.5.14", {"start": v(43.75, -42.25) * mm, "mid": v(43.46, -41.54) * mm, "end": v(42.75, -41.25) * mm});
            skLineSegment(sketch, "E13.4.0.0", {"start": v(73.75, 57.75) * mm, "end": v(73.75, 42.25) * mm});
            skLineSegment(sketch, "E13.4.0.1", {"start": v(47.25, 58.75) * mm, "end": v(72.75, 58.75) * mm});
            skLineSegment(sketch, "E13.4.0.3", {"start": v(47.25, 41.25) * mm, "end": v(72.75, 41.25) * mm});
            skPoint(sketch, "E13.4.0.5", {"position": v(73.75, 41.25) * mm});
            skLineSegment(sketch, "E13.4.0.6", {"start": v(46.25, 57.75) * mm, "end": v(46.25, 42.25) * mm});
            skPoint(sketch, "E13.4.0.8", {"position": v(46.25, 58.75) * mm});
            skPoint(sketch, "E13.4.0.10", {"position": v(41.25, 63.75) * mm});
            skArc(sketch, "E13.4.0.11", {"start": v(46.25, 42.25) * mm, "mid": v(46.54, 41.54) * mm, "end": v(47.25, 41.25) * mm});
            skArc(sketch, "E13.4.0.12", {"start": v(72.75, 41.25) * mm, "mid": v(73.46, 41.54) * mm, "end": v(73.75, 42.25) * mm});
            skArc(sketch, "E13.4.0.13", {"start": v(47.25, 58.75) * mm, "mid": v(46.54, 58.46) * mm, "end": v(46.25, 57.75) * mm});
            skLineSegment(sketch, "E13.4.1.0", {"start": v(73.75, 37.75) * mm, "end": v(73.75, 22.25) * mm});
            skLineSegment(sketch, "E13.4.1.1", {"start": v(47.25, 38.75) * mm, "end": v(72.75, 38.75) * mm});
            skPoint(sketch, "E13.4.1.2", {"position": v(46.25, 21.25) * mm});
            skLineSegment(sketch, "E13.4.1.3", {"start": v(47.25, 21.25) * mm, "end": v(72.75, 21.25) * mm});
            skPoint(sketch, "E13.4.1.5", {"position": v(73.75, 21.25) * mm});
            skLineSegment(sketch, "E13.4.1.6", {"start": v(46.25, 37.75) * mm, "end": v(46.25, 22.25) * mm});
            skPoint(sketch, "E13.4.1.7", {"position": v(73.75, 38.75) * mm});
            skPoint(sketch, "E13.4.1.8", {"position": v(46.25, 38.75) * mm});
            skPoint(sketch, "E13.4.1.10", {"position": v(41.25, 43.75) * mm});
            skArc(sketch, "E13.4.1.11", {"start": v(46.25, 22.25) * mm, "mid": v(46.54, 21.54) * mm, "end": v(47.25, 21.25) * mm});
            skArc(sketch, "E13.4.1.12", {"start": v(72.75, 21.25) * mm, "mid": v(73.46, 21.54) * mm, "end": v(73.75, 22.25) * mm});
            skArc(sketch, "E13.4.1.13", {"start": v(47.25, 38.75) * mm, "mid": v(46.54, 38.46) * mm, "end": v(46.25, 37.75) * mm});
            skArc(sketch, "E13.4.1.14", {"start": v(73.75, 37.75) * mm, "mid": v(73.46, 38.46) * mm, "end": v(72.75, 38.75) * mm});
            skLineSegment(sketch, "E13.4.2.0", {"start": v(73.75, 17.75) * mm, "end": v(73.75, 2.25) * mm});
            skLineSegment(sketch, "E13.4.2.1", {"start": v(47.25, 18.75) * mm, "end": v(72.75, 18.75) * mm});
            skPoint(sketch, "E13.4.2.2", {"position": v(46.25, 1.25) * mm});
            skLineSegment(sketch, "E13.4.2.3", {"start": v(47.25, 1.25) * mm, "end": v(72.75, 1.25) * mm});
            skPoint(sketch, "E13.4.2.5", {"position": v(73.75, 1.25) * mm});
            skLineSegment(sketch, "E13.4.2.6", {"start": v(46.25, 17.75) * mm, "end": v(46.25, 2.25) * mm});
            skPoint(sketch, "E13.4.2.7", {"position": v(73.75, 18.75) * mm});
            skPoint(sketch, "E13.4.2.8", {"position": v(46.25, 18.75) * mm});
            skPoint(sketch, "E13.4.2.10", {"position": v(41.25, 23.75) * mm});
            skArc(sketch, "E13.4.2.11", {"start": v(46.25, 2.25) * mm, "mid": v(46.54, 1.54) * mm, "end": v(47.25, 1.25) * mm});
            skArc(sketch, "E13.4.2.12", {"start": v(72.75, 1.25) * mm, "mid": v(73.46, 1.54) * mm, "end": v(73.75, 2.25) * mm});
            skArc(sketch, "E13.4.2.13", {"start": v(47.25, 18.75) * mm, "mid": v(46.54, 18.46) * mm, "end": v(46.25, 17.75) * mm});
            skArc(sketch, "E13.4.2.14", {"start": v(73.75, 17.75) * mm, "mid": v(73.46, 18.46) * mm, "end": v(72.75, 18.75) * mm});
            skLineSegment(sketch, "E13.4.3.0", {"start": v(73.75, -2.25) * mm, "end": v(73.75, -17.75) * mm});
            skLineSegment(sketch, "E13.4.3.1", {"start": v(47.25, -1.25) * mm, "end": v(72.75, -1.25) * mm});
            skPoint(sketch, "E13.4.3.2", {"position": v(46.25, -18.75) * mm});
            skLineSegment(sketch, "E13.4.3.3", {"start": v(47.25, -18.75) * mm, "end": v(72.75, -18.75) * mm});
            skPoint(sketch, "E13.4.3.5", {"position": v(73.75, -18.75) * mm});
            skLineSegment(sketch, "E13.4.3.6", {"start": v(46.25, -2.25) * mm, "end": v(46.25, -17.75) * mm});
            skPoint(sketch, "E13.4.3.7", {"position": v(73.75, -1.25) * mm});
            skPoint(sketch, "E13.4.3.8", {"position": v(46.25, -1.25) * mm});
            skPoint(sketch, "E13.4.3.10", {"position": v(41.25, 3.75) * mm});
            skArc(sketch, "E13.4.3.11", {"start": v(46.25, -17.75) * mm, "mid": v(46.54, -18.46) * mm, "end": v(47.25, -18.75) * mm});
            skArc(sketch, "E13.4.3.12", {"start": v(72.75, -18.75) * mm, "mid": v(73.46, -18.46) * mm, "end": v(73.75, -17.75) * mm});
            skArc(sketch, "E13.4.3.13", {"start": v(47.25, -1.25) * mm, "mid": v(46.54, -1.54) * mm, "end": v(46.25, -2.25) * mm});
            skArc(sketch, "E13.4.3.14", {"start": v(73.75, -2.25) * mm, "mid": v(73.46, -1.54) * mm, "end": v(72.75, -1.25) * mm});
            skLineSegment(sketch, "E13.4.4.0", {"start": v(73.75, -22.25) * mm, "end": v(73.75, -37.75) * mm});
            skLineSegment(sketch, "E13.4.4.1", {"start": v(47.25, -21.25) * mm, "end": v(72.75, -21.25) * mm});
            skPoint(sketch, "E13.4.4.2", {"position": v(46.25, -38.75) * mm});
            skLineSegment(sketch, "E13.4.4.3", {"start": v(47.25, -38.75) * mm, "end": v(72.75, -38.75) * mm});
            skPoint(sketch, "E13.4.4.5", {"position": v(73.75, -38.75) * mm});
            skLineSegment(sketch, "E13.4.4.6", {"start": v(46.25, -22.25) * mm, "end": v(46.25, -37.75) * mm});
            skPoint(sketch, "E13.4.4.7", {"position": v(73.75, -21.25) * mm});
            skPoint(sketch, "E13.4.4.8", {"position": v(46.25, -21.25) * mm});
            skPoint(sketch, "E13.4.4.10", {"position": v(41.25, -16.25) * mm});
            skArc(sketch, "E13.4.4.11", {"start": v(46.25, -37.75) * mm, "mid": v(46.54, -38.46) * mm, "end": v(47.25, -38.75) * mm});
            skArc(sketch, "E13.4.4.12", {"start": v(72.75, -38.75) * mm, "mid": v(73.46, -38.46) * mm, "end": v(73.75, -37.75) * mm});
            skArc(sketch, "E13.4.4.13", {"start": v(47.25, -21.25) * mm, "mid": v(46.54, -21.54) * mm, "end": v(46.25, -22.25) * mm});
            skArc(sketch, "E13.4.4.14", {"start": v(73.75, -22.25) * mm, "mid": v(73.46, -21.54) * mm, "end": v(72.75, -21.25) * mm});
            skLineSegment(sketch, "E13.4.5.0", {"start": v(73.75, -42.25) * mm, "end": v(73.75, -57.75) * mm});
            skLineSegment(sketch, "E13.4.5.1", {"start": v(47.25, -41.25) * mm, "end": v(72.75, -41.25) * mm});
            skLineSegment(sketch, "E13.4.5.3", {"start": v(47.25, -58.75) * mm, "end": v(72.75, -58.75) * mm});
            skPoint(sketch, "E13.4.5.5", {"position": v(73.75, -58.75) * mm});
            skLineSegment(sketch, "E13.4.5.6", {"start": v(46.25, -42.25) * mm, "end": v(46.25, -57.75) * mm});
            skPoint(sketch, "E13.4.5.7", {"position": v(73.75, -41.25) * mm});
            skPoint(sketch, "E13.4.5.8", {"position": v(46.25, -41.25) * mm});
            skPoint(sketch, "E13.4.5.10", {"position": v(41.25, -36.25) * mm});
            skArc(sketch, "E13.4.5.11", {"start": v(46.25, -57.75) * mm, "mid": v(46.54, -58.46) * mm, "end": v(47.25, -58.75) * mm});
            skArc(sketch, "E13.4.5.12", {"start": v(72.75, -58.75) * mm, "mid": v(73.46, -58.46) * mm, "end": v(73.75, -57.75) * mm});
            skArc(sketch, "E13.4.5.13", {"start": v(47.25, -41.25) * mm, "mid": v(46.54, -41.54) * mm, "end": v(46.25, -42.25) * mm});
            skArc(sketch, "E13.4.5.14", {"start": v(73.75, -42.25) * mm, "mid": v(73.46, -41.54) * mm, "end": v(72.75, -41.25) * mm});
            skLineSegment(sketch, "E13.direction1", {"start": v(-46.25, 42.25) * mm, "end": v(-16.25, 42.25) * mm, "construction": true});
            skLineSegment(sketch, "E13.direction2", {"start": v(-46.25, 42.25) * mm, "end": v(-46.25, 22.25) * mm, "construction": true});
            skPoint(sketch, "E14.newPointA", {"position": v(72.75, 58.75) * mm});
            skPoint(sketch, "E14.newPointB", {"position": v(73.75, 57.75) * mm});
            skArc(sketch, "E14.filletArc", {"start": v(73.75, 57.75) * mm, "mid": v(73.46, 58.46) * mm, "end": v(72.75, 58.75) * mm});
            skSolve(sketch);
        }
        {
            var Q0;
            Q0 = qSketchRegion(id + "F0", true);
            extrude(context, id + "F2", {"entities" : qUnion([Q0]), "depth" : 38 * mm, "hasSecondDirection" : true, "secondDirectionOppositeDirection" : true, "secondDirectionDepth" : 3 * mm});
        }
        {
            var Q0;
            Q0 = qSketchRegion(id + "F1", true);
            extrude(context, id + "F3", {"entities" : qUnion([Q0]), "operationType" : NewBodyOperationType.REMOVE, "depth" : 45 * mm});
        }
        {
            var Q0;
            Q0=makeQuery(id+"F2.opExtrude","SWEPT_FACE",FACE,{"disambiguationData":[OSD([sQuery(id+"F0.wireOp",EDGE,"E0.rect.bottom")])]});
            var sketch = newSketch(context, id + "F4", { "sketchPlane" : qUnion([Q0])});
            skLineSegment(sketch, "E15", {"start": v(-69, 38) * mm, "end": v(-51, 38) * mm});
            skLineSegment(sketch, "E16", {"start": v(0, 38) * mm, "end": v(0, 30.13) * mm});
            skLineSegment(sketch, "E17.0", {"start": v(30, 38) * mm, "end": v(30, 30.13) * mm});
            skLineSegment(sketch, "E18.0", {"start": v(60, 38) * mm, "end": v(60, 30.13) * mm});
            skLineSegment(sketch, "E19.0", {"start": v(-30, 38) * mm, "end": v(-30, 30.13) * mm});
            skLineSegment(sketch, "E20.0", {"start": v(-60, 38) * mm, "end": v(-60, 30.13) * mm});
            skArc(sketch, "E21", {"start": v(-69, 38) * mm, "mid": v(-60, 29) * mm, "end": v(-51, 38) * mm});
            skArc(sketch, "E22.1.0.0", {"start": v(-39, 38) * mm, "mid": v(-30, 29) * mm, "end": v(-21, 38) * mm});
            skArc(sketch, "E22.2.0.0", {"start": v(-9, 38) * mm, "mid": v(0, 29) * mm, "end": v(9, 38) * mm});
            skArc(sketch, "E22.3.0.0", {"start": v(21, 38) * mm, "mid": v(30, 29) * mm, "end": v(39, 38) * mm});
            skArc(sketch, "E22.4.0.0", {"start": v(51, 38) * mm, "mid": v(60, 29) * mm, "end": v(69, 38) * mm});
            skLineSegment(sketch, "E22.direction1", {"start": v(-60, 38) * mm, "end": v(-30, 38) * mm, "construction": true});
            skLineSegment(sketch, "E23.trimOffspring", {"start": v(-39, 38) * mm, "end": v(-21, 38) * mm});
            skLineSegment(sketch, "E24.trimOffspring", {"start": v(-9, 38) * mm, "end": v(9, 38) * mm});
            skLineSegment(sketch, "E25.trimOffspring", {"start": v(21, 38) * mm, "end": v(39, 38) * mm});
            skLineSegment(sketch, "E26.trimOffspring", {"start": v(51, 38) * mm, "end": v(69, 38) * mm});
            skArc(sketch, "E27", {"start": v(-69, 12) * mm, "mid": v(-60, 3) * mm, "end": v(-51, 12) * mm});
            skArc(sketch, "E28.trimOffspring", {"start": v(-51, 17) * mm, "mid": v(-60, 26) * mm, "end": v(-69, 17) * mm});
            skLineSegment(sketch, "E29", {"start": v(-69, 17) * mm, "end": v(-69, 12) * mm});
            skLineSegment(sketch, "E30", {"start": v(-51, 17) * mm, "end": v(-51, 12) * mm});
            skArc(sketch, "E31.1.0.0", {"start": v(-21, 17) * mm, "mid": v(-30, 26) * mm, "end": v(-39, 17) * mm});
            skLineSegment(sketch, "E31.1.0.1", {"start": v(-21, 17) * mm, "end": v(-21, 12) * mm});
            skLineSegment(sketch, "E31.1.0.2", {"start": v(-39, 17) * mm, "end": v(-39, 12) * mm});
            skArc(sketch, "E31.1.0.3", {"start": v(-39, 12) * mm, "mid": v(-30, 3) * mm, "end": v(-21, 12) * mm});
            skArc(sketch, "E31.2.0.0", {"start": v(9, 17) * mm, "mid": v(0, 26) * mm, "end": v(-9, 17) * mm});
            skLineSegment(sketch, "E31.2.0.1", {"start": v(9, 17) * mm, "end": v(9, 12) * mm});
            skLineSegment(sketch, "E31.2.0.2", {"start": v(-9, 17) * mm, "end": v(-9, 12) * mm});
            skArc(sketch, "E31.2.0.3", {"start": v(-9, 12) * mm, "mid": v(0, 3) * mm, "end": v(9, 12) * mm});
            skArc(sketch, "E31.3.0.0", {"start": v(39, 17) * mm, "mid": v(30, 26) * mm, "end": v(21, 17) * mm});
            skLineSegment(sketch, "E31.3.0.1", {"start": v(39, 17) * mm, "end": v(39, 12) * mm});
            skLineSegment(sketch, "E31.3.0.2", {"start": v(21, 17) * mm, "end": v(21, 12) * mm});
            skArc(sketch, "E31.3.0.3", {"start": v(21, 12) * mm, "mid": v(30, 3) * mm, "end": v(39, 12) * mm});
            skArc(sketch, "E31.4.0.0", {"start": v(69, 17) * mm, "mid": v(60, 26) * mm, "end": v(51, 17) * mm});
            skLineSegment(sketch, "E31.4.0.1", {"start": v(69, 17) * mm, "end": v(69, 12) * mm});
            skLineSegment(sketch, "E31.4.0.2", {"start": v(51, 17) * mm, "end": v(51, 12) * mm});
            skArc(sketch, "E31.4.0.3", {"start": v(51, 12) * mm, "mid": v(60, 3) * mm, "end": v(69, 12) * mm});
            skLineSegment(sketch, "E31.direction1", {"start": v(-69, 17) * mm, "end": v(-39, 17) * mm, "construction": true});
            skSolve(sketch);
        }
        {
            var Q0;
            Q0 = qSketchRegion(id + "F4", true);
            extrude(context, id + "F5", {"entities" : qUnion([Q0]), "operationType" : NewBodyOperationType.REMOVE, "endBound" : BoundingType.THROUGH_ALL, "oppositeDirection" : true, "depth" : 25 * mm});
        }
        {
            var Q0;
            Q0=makeQuery(id+"F2.opExtrude","SWEPT_FACE",FACE,{"disambiguationData":[OSD([sQuery(id+"F0.wireOp",EDGE,"E0.rect.left")])]});
            var sketch = newSketch(context, id + "F6", { "sketchPlane" : qUnion([Q0])});
            skArc(sketch, "E32", {"start": v(-44, 28.03) * mm, "mid": v(-50, 34.03) * mm, "end": v(-56, 28.03) * mm});
            skArc(sketch, "E33", {"start": v(-56, 10) * mm, "mid": v(-50, 4) * mm, "end": v(-44, 10) * mm});
            skLineSegment(sketch, "E34", {"start": v(-56, 28.03) * mm, "end": v(-56, 10) * mm});
            skLineSegment(sketch, "E35", {"start": v(-44, 28.03) * mm, "end": v(-44, 10) * mm});
            skArc(sketch, "E36.1.0.0", {"start": v(-36, 10) * mm, "mid": v(-30, 4) * mm, "end": v(-24, 10) * mm});
            skLineSegment(sketch, "E36.1.0.1", {"start": v(-36, 28.03) * mm, "end": v(-36, 10) * mm});
            skLineSegment(sketch, "E36.1.0.7", {"start": v(-24, 28.03) * mm, "end": v(-24, 10) * mm});
            skArc(sketch, "E36.1.0.9", {"start": v(-24, 28.03) * mm, "mid": v(-30, 34.03) * mm, "end": v(-36, 28.03) * mm});
            skArc(sketch, "E36.2.0.0", {"start": v(-16, 10) * mm, "mid": v(-10, 4) * mm, "end": v(-4, 10) * mm});
            skLineSegment(sketch, "E36.2.0.1", {"start": v(-16, 28.03) * mm, "end": v(-16, 10) * mm});
            skLineSegment(sketch, "E36.2.0.7", {"start": v(-4, 28.03) * mm, "end": v(-4, 10) * mm});
            skArc(sketch, "E36.2.0.9", {"start": v(-4, 28.03) * mm, "mid": v(-10, 34.03) * mm, "end": v(-16, 28.03) * mm});
            skArc(sketch, "E36.3.0.0", {"start": v(4, 10) * mm, "mid": v(10, 4) * mm, "end": v(16, 10) * mm});
            skLineSegment(sketch, "E36.3.0.1", {"start": v(4, 28.03) * mm, "end": v(4, 10) * mm});
            skLineSegment(sketch, "E36.3.0.7", {"start": v(16, 28.03) * mm, "end": v(16, 10) * mm});
            skArc(sketch, "E36.3.0.9", {"start": v(16, 28.03) * mm, "mid": v(10, 34.03) * mm, "end": v(4, 28.03) * mm});
            skArc(sketch, "E36.4.0.0", {"start": v(24, 10) * mm, "mid": v(30, 4) * mm, "end": v(36, 10) * mm});
            skLineSegment(sketch, "E36.4.0.1", {"start": v(24, 28.03) * mm, "end": v(24, 10) * mm});
            skLineSegment(sketch, "E36.4.0.7", {"start": v(36, 28.03) * mm, "end": v(36, 10) * mm});
            skArc(sketch, "E36.4.0.9", {"start": v(36, 28.03) * mm, "mid": v(30, 34.03) * mm, "end": v(24, 28.03) * mm});
            skArc(sketch, "E36.5.0.0", {"start": v(44, 10) * mm, "mid": v(50, 4) * mm, "end": v(56, 10) * mm});
            skLineSegment(sketch, "E36.5.0.1", {"start": v(44, 28.03) * mm, "end": v(44, 10) * mm});
            skLineSegment(sketch, "E36.5.0.7", {"start": v(56, 28.03) * mm, "end": v(56, 10) * mm});
            skArc(sketch, "E36.5.0.9", {"start": v(56, 28.03) * mm, "mid": v(50, 34.03) * mm, "end": v(44, 28.03) * mm});
            skArc(sketch, "E36.6.0.0", {"start": v(64, 10) * mm, "mid": v(70, 4) * mm, "end": v(76, 10) * mm});
            skLineSegment(sketch, "E36.6.0.1", {"start": v(64, 28.03) * mm, "end": v(64, 10) * mm});
            skLineSegment(sketch, "E36.6.0.7", {"start": v(76, 28.03) * mm, "end": v(76, 10) * mm});
            skArc(sketch, "E36.6.0.9", {"start": v(76, 28.03) * mm, "mid": v(70, 34.03) * mm, "end": v(64, 28.03) * mm});
            skSolve(sketch);
        }
        {
            var Q0;
            Q0 = qSketchRegion(id + "F6", true);
            extrude(context, id + "F7", {"entities" : qUnion([Q0]), "operationType" : NewBodyOperationType.REMOVE, "endBound" : BoundingType.THROUGH_ALL, "oppositeDirection" : true, "depth" : 25 * mm});
        }
        {
            var Q0;
            Q0=makeQuery(id+"F2.opExtrude","SWEPT_FACE",FACE,{"disambiguationData":[OSD([sQuery(id+"F0.wireOp",EDGE,"E0.rect.left")])]});
            var Q1;
            Q1=makeQuery(id+"F2.opExtrude","SWEPT_FACE",FACE,{"disambiguationData":[OSD([sQuery(id+"F0.wireOp",EDGE,"E0.rect.bottom")])]});
            var Q2;
            Q2=makeQuery(id+"F2.opExtrude","SWEPT_FACE",FACE,{"disambiguationData":[OSD([sQuery(id+"F0.wireOp",EDGE,"E0.rect.right")])]});
            var Q3;
            Q3=makeQuery(id+"F2.opExtrude","SWEPT_FACE",FACE,{"disambiguationData":[OSD([sQuery(id+"F0.wireOp",EDGE,"E0.rect.top")])]});
            var Q4;
            Q4=makeQuery(id+"F2.opExtrude","CAP_FACE",FACE,{"disambiguationData":[OSD([sQuery(id+"F0.wireOp",EDGE,"E0.rect.bottom"),sQuery(id+"F0.wireOp",EDGE,"E0.rect.top"),sQuery(id+"F0.wireOp",EDGE,"E0.rect.left"),sQuery(id+"F0.wireOp",EDGE,"E0.rect.right"),sQuery(id+"F0.wireOp",EDGE,"E1"),sQuery(id+"F0.wireOp",EDGE,"E2.0.1.0"),sQuery(id+"F0.wireOp",EDGE,"E2.0.2.0"),sQuery(id+"F0.wireOp",EDGE,"E2.0.3.0"),sQuery(id+"F0.wireOp",EDGE,"E2.0.4.0"),sQuery(id+"F0.wireOp",EDGE,"E2.0.5.0"),sQuery(id+"F0.wireOp",EDGE,"E2.1.0.0"),sQuery(id+"F0.wireOp",EDGE,"E2.1.1.0"),sQuery(id+"F0.wireOp",EDGE,"E2.1.2.0"),sQuery(id+"F0.wireOp",EDGE,"E2.1.3.0"),sQuery(id+"F0.wireOp",EDGE,"E2.1.4.0"),sQuery(id+"F0.wireOp",EDGE,"E2.1.5.0"),sQuery(id+"F0.wireOp",EDGE,"E2.2.0.0"),sQuery(id+"F0.wireOp",EDGE,"E2.2.1.0"),sQuery(id+"F0.wireOp",EDGE,"E2.2.2.0"),sQuery(id+"F0.wireOp",EDGE,"E2.2.3.0"),sQuery(id+"F0.wireOp",EDGE,"E2.2.4.0"),sQuery(id+"F0.wireOp",EDGE,"E2.2.5.0"),sQuery(id+"F0.wireOp",EDGE,"E2.3.0.0"),sQuery(id+"F0.wireOp",EDGE,"E2.3.1.0"),sQuery(id+"F0.wireOp",EDGE,"E2.3.2.0"),sQuery(id+"F0.wireOp",EDGE,"E2.3.3.0"),sQuery(id+"F0.wireOp",EDGE,"E2.3.4.0"),sQuery(id+"F0.wireOp",EDGE,"E2.3.5.0"),sQuery(id+"F0.wireOp",EDGE,"E2.4.0.0"),sQuery(id+"F0.wireOp",EDGE,"E2.4.1.0"),sQuery(id+"F0.wireOp",EDGE,"E2.4.2.0"),sQuery(id+"F0.wireOp",EDGE,"E2.4.3.0"),sQuery(id+"F0.wireOp",EDGE,"E2.4.4.0"),sQuery(id+"F0.wireOp",EDGE,"E2.4.5.0"),sQuery(id+"F0.wireOp",EDGE,"E3.filletArc"),sQuery(id+"F0.wireOp",EDGE,"E4.filletArc"),sQuery(id+"F0.wireOp",EDGE,"E5.filletArc"),sQuery(id+"F0.wireOp",EDGE,"E6.filletArc")])],"isStart":true});
            fillet(context, id + "F8", {"entities" : qUnion([Q0, Q1, Q2, Q3, Q4]), "radius" : 2 * mm, "tangentPropagation" : true, "allowEdgeOverflow" : false});
        }
        {
            var Q0;
            {var subQ0=sQuery(id+"F0.wireOp",EDGE,"E0.rect.bottom");var subQ1=sQuery(id+"F0.wireOp",EDGE,"E0.rect.top");var subQ2=sQuery(id+"F0.wireOp",EDGE,"E0.rect.right");var subQ3=sQuery(id+"F0.wireOp",EDGE,"E5.filletArc");var subQ4=sQuery(id+"F0.wireOp",EDGE,"E6.filletArc");Q0=makeQuery(id+"F5.boolean.opBoolean","SPLIT",FACE,{"disambiguationData":[TD([makeQuery(id+"F2.opExtrude","SWEPT_FACE",FACE,{"disambiguationData":[OSD([subQ2])]})])],"derivedFrom":makeQuery(id+"F2.opExtrude","CAP_FACE",FACE,{"disambiguationData":[OSD([subQ0,subQ1,sQuery(id+"F0.wireOp",EDGE,"E0.rect.left"),subQ2,sQuery(id+"F0.wireOp",EDGE,"E1"),sQuery(id+"F0.wireOp",EDGE,"E2.0.1.0"),sQuery(id+"F0.wireOp",EDGE,"E2.0.2.0"),sQuery(id+"F0.wireOp",EDGE,"E2.0.3.0"),sQuery(id+"F0.wireOp",EDGE,"E2.0.4.0"),sQuery(id+"F0.wireOp",EDGE,"E2.0.5.0"),sQuery(id+"F0.wireOp",EDGE,"E2.1.0.0"),sQuery(id+"F0.wireOp",EDGE,"E2.1.1.0"),sQuery(id+"F0.wireOp",EDGE,"E2.1.2.0"),sQuery(id+"F0.wireOp",EDGE,"E2.1.3.0"),sQuery(id+"F0.wireOp",EDGE,"E2.1.4.0"),sQuery(id+"F0.wireOp",EDGE,"E2.1.5.0"),sQuery(id+"F0.wireOp",EDGE,"E2.2.0.0"),sQuery(id+"F0.wireOp",EDGE,"E2.2.1.0"),sQuery(id+"F0.wireOp",EDGE,"E2.2.2.0"),sQuery(id+"F0.wireOp",EDGE,"E2.2.3.0"),sQuery(id+"F0.wireOp",EDGE,"E2.2.4.0"),sQuery(id+"F0.wireOp",EDGE,"E2.2.5.0"),sQuery(id+"F0.wireOp",EDGE,"E2.3.0.0"),sQuery(id+"F0.wireOp",EDGE,"E2.3.1.0"),sQuery(id+"F0.wireOp",EDGE,"E2.3.2.0"),sQuery(id+"F0.wireOp",EDGE,"E2.3.3.0"),sQuery(id+"F0.wireOp",EDGE,"E2.3.4.0"),sQuery(id+"F0.wireOp",EDGE,"E2.3.5.0"),sQuery(id+"F0.wireOp",EDGE,"E2.4.0.0"),sQuery(id+"F0.wireOp",EDGE,"E2.4.1.0"),sQuery(id+"F0.wireOp",EDGE,"E2.4.2.0"),sQuery(id+"F0.wireOp",EDGE,"E2.4.3.0"),sQuery(id+"F0.wireOp",EDGE,"E2.4.4.0"),sQuery(id+"F0.wireOp",EDGE,"E2.4.5.0"),sQuery(id+"F0.wireOp",EDGE,"E3.filletArc"),sQuery(id+"F0.wireOp",EDGE,"E4.filletArc"),subQ3,subQ4])],"isStart":false})});}
            var Q1;
            {var subQ0=sQuery(id+"F0.wireOp",EDGE,"E0.rect.bottom");var subQ1=sQuery(id+"F0.wireOp",EDGE,"E0.rect.top");Q1=makeQuery(id+"F5.boolean.opBoolean","SPLIT",FACE,{"disambiguationData":[TD([makeQuery(id+"F3.boolean.opBoolean","COPY",FACE,{"derivedFrom":makeQuery(id+"F3.opExtrude","SWEPT_FACE",FACE,{"disambiguationData":[OSD([sQuery(id+"F1.wireOp",EDGE,"E8.right")])]})})])],"derivedFrom":makeQuery(id+"F2.opExtrude","CAP_FACE",FACE,{"disambiguationData":[OSD([subQ0,subQ1,sQuery(id+"F0.wireOp",EDGE,"E0.rect.left"),sQuery(id+"F0.wireOp",EDGE,"E0.rect.right"),sQuery(id+"F0.wireOp",EDGE,"E1"),sQuery(id+"F0.wireOp",EDGE,"E2.0.1.0"),sQuery(id+"F0.wireOp",EDGE,"E2.0.2.0"),sQuery(id+"F0.wireOp",EDGE,"E2.0.3.0"),sQuery(id+"F0.wireOp",EDGE,"E2.0.4.0"),sQuery(id+"F0.wireOp",EDGE,"E2.0.5.0"),sQuery(id+"F0.wireOp",EDGE,"E2.1.0.0"),sQuery(id+"F0.wireOp",EDGE,"E2.1.1.0"),sQuery(id+"F0.wireOp",EDGE,"E2.1.2.0"),sQuery(id+"F0.wireOp",EDGE,"E2.1.3.0"),sQuery(id+"F0.wireOp",EDGE,"E2.1.4.0"),sQuery(id+"F0.wireOp",EDGE,"E2.1.5.0"),sQuery(id+"F0.wireOp",EDGE,"E2.2.0.0"),sQuery(id+"F0.wireOp",EDGE,"E2.2.1.0"),sQuery(id+"F0.wireOp",EDGE,"E2.2.2.0"),sQuery(id+"F0.wireOp",EDGE,"E2.2.3.0"),sQuery(id+"F0.wireOp",EDGE,"E2.2.4.0"),sQuery(id+"F0.wireOp",EDGE,"E2.2.5.0"),sQuery(id+"F0.wireOp",EDGE,"E2.3.0.0"),sQuery(id+"F0.wireOp",EDGE,"E2.3.1.0"),sQuery(id+"F0.wireOp",EDGE,"E2.3.2.0"),sQuery(id+"F0.wireOp",EDGE,"E2.3.3.0"),sQuery(id+"F0.wireOp",EDGE,"E2.3.4.0"),sQuery(id+"F0.wireOp",EDGE,"E2.3.5.0"),sQuery(id+"F0.wireOp",EDGE,"E2.4.0.0"),sQuery(id+"F0.wireOp",EDGE,"E2.4.1.0"),sQuery(id+"F0.wireOp",EDGE,"E2.4.2.0"),sQuery(id+"F0.wireOp",EDGE,"E2.4.3.0"),sQuery(id+"F0.wireOp",EDGE,"E2.4.4.0"),sQuery(id+"F0.wireOp",EDGE,"E2.4.5.0"),sQuery(id+"F0.wireOp",EDGE,"E3.filletArc"),sQuery(id+"F0.wireOp",EDGE,"E4.filletArc"),sQuery(id+"F0.wireOp",EDGE,"E5.filletArc"),sQuery(id+"F0.wireOp",EDGE,"E6.filletArc")])],"isStart":false})});}
            var Q2;
            {var subQ0=sQuery(id+"F0.wireOp",EDGE,"E0.rect.bottom");var subQ1=sQuery(id+"F0.wireOp",EDGE,"E0.rect.top");Q2=makeQuery(id+"F5.boolean.opBoolean","SPLIT",FACE,{"disambiguationData":[TD([makeQuery(id+"F3.boolean.opBoolean","COPY",FACE,{"derivedFrom":makeQuery(id+"F3.opExtrude","SWEPT_FACE",FACE,{"disambiguationData":[OSD([sQuery(id+"F1.wireOp",EDGE,"E13.1.0.0")])]})})])],"derivedFrom":makeQuery(id+"F2.opExtrude","CAP_FACE",FACE,{"disambiguationData":[OSD([subQ0,subQ1,sQuery(id+"F0.wireOp",EDGE,"E0.rect.left"),sQuery(id+"F0.wireOp",EDGE,"E0.rect.right"),sQuery(id+"F0.wireOp",EDGE,"E1"),sQuery(id+"F0.wireOp",EDGE,"E2.0.1.0"),sQuery(id+"F0.wireOp",EDGE,"E2.0.2.0"),sQuery(id+"F0.wireOp",EDGE,"E2.0.3.0"),sQuery(id+"F0.wireOp",EDGE,"E2.0.4.0"),sQuery(id+"F0.wireOp",EDGE,"E2.0.5.0"),sQuery(id+"F0.wireOp",EDGE,"E2.1.0.0"),sQuery(id+"F0.wireOp",EDGE,"E2.1.1.0"),sQuery(id+"F0.wireOp",EDGE,"E2.1.2.0"),sQuery(id+"F0.wireOp",EDGE,"E2.1.3.0"),sQuery(id+"F0.wireOp",EDGE,"E2.1.4.0"),sQuery(id+"F0.wireOp",EDGE,"E2.1.5.0"),sQuery(id+"F0.wireOp",EDGE,"E2.2.0.0"),sQuery(id+"F0.wireOp",EDGE,"E2.2.1.0"),sQuery(id+"F0.wireOp",EDGE,"E2.2.2.0"),sQuery(id+"F0.wireOp",EDGE,"E2.2.3.0"),sQuery(id+"F0.wireOp",EDGE,"E2.2.4.0"),sQuery(id+"F0.wireOp",EDGE,"E2.2.5.0"),sQuery(id+"F0.wireOp",EDGE,"E2.3.0.0"),sQuery(id+"F0.wireOp",EDGE,"E2.3.1.0"),sQuery(id+"F0.wireOp",EDGE,"E2.3.2.0"),sQuery(id+"F0.wireOp",EDGE,"E2.3.3.0"),sQuery(id+"F0.wireOp",EDGE,"E2.3.4.0"),sQuery(id+"F0.wireOp",EDGE,"E2.3.5.0"),sQuery(id+"F0.wireOp",EDGE,"E2.4.0.0"),sQuery(id+"F0.wireOp",EDGE,"E2.4.1.0"),sQuery(id+"F0.wireOp",EDGE,"E2.4.2.0"),sQuery(id+"F0.wireOp",EDGE,"E2.4.3.0"),sQuery(id+"F0.wireOp",EDGE,"E2.4.4.0"),sQuery(id+"F0.wireOp",EDGE,"E2.4.5.0"),sQuery(id+"F0.wireOp",EDGE,"E3.filletArc"),sQuery(id+"F0.wireOp",EDGE,"E4.filletArc"),sQuery(id+"F0.wireOp",EDGE,"E5.filletArc"),sQuery(id+"F0.wireOp",EDGE,"E6.filletArc")])],"isStart":false})});}
            var Q3;
            {var subQ0=sQuery(id+"F0.wireOp",EDGE,"E0.rect.bottom");var subQ1=sQuery(id+"F0.wireOp",EDGE,"E0.rect.top");Q3=makeQuery(id+"F5.boolean.opBoolean","SPLIT",FACE,{"disambiguationData":[TD([makeQuery(id+"F3.boolean.opBoolean","COPY",FACE,{"derivedFrom":makeQuery(id+"F3.opExtrude","SWEPT_FACE",FACE,{"disambiguationData":[OSD([sQuery(id+"F1.wireOp",EDGE,"E13.2.0.0")])]})})])],"derivedFrom":makeQuery(id+"F2.opExtrude","CAP_FACE",FACE,{"disambiguationData":[OSD([subQ0,subQ1,sQuery(id+"F0.wireOp",EDGE,"E0.rect.left"),sQuery(id+"F0.wireOp",EDGE,"E0.rect.right"),sQuery(id+"F0.wireOp",EDGE,"E1"),sQuery(id+"F0.wireOp",EDGE,"E2.0.1.0"),sQuery(id+"F0.wireOp",EDGE,"E2.0.2.0"),sQuery(id+"F0.wireOp",EDGE,"E2.0.3.0"),sQuery(id+"F0.wireOp",EDGE,"E2.0.4.0"),sQuery(id+"F0.wireOp",EDGE,"E2.0.5.0"),sQuery(id+"F0.wireOp",EDGE,"E2.1.0.0"),sQuery(id+"F0.wireOp",EDGE,"E2.1.1.0"),sQuery(id+"F0.wireOp",EDGE,"E2.1.2.0"),sQuery(id+"F0.wireOp",EDGE,"E2.1.3.0"),sQuery(id+"F0.wireOp",EDGE,"E2.1.4.0"),sQuery(id+"F0.wireOp",EDGE,"E2.1.5.0"),sQuery(id+"F0.wireOp",EDGE,"E2.2.0.0"),sQuery(id+"F0.wireOp",EDGE,"E2.2.1.0"),sQuery(id+"F0.wireOp",EDGE,"E2.2.2.0"),sQuery(id+"F0.wireOp",EDGE,"E2.2.3.0"),sQuery(id+"F0.wireOp",EDGE,"E2.2.4.0"),sQuery(id+"F0.wireOp",EDGE,"E2.2.5.0"),sQuery(id+"F0.wireOp",EDGE,"E2.3.0.0"),sQuery(id+"F0.wireOp",EDGE,"E2.3.1.0"),sQuery(id+"F0.wireOp",EDGE,"E2.3.2.0"),sQuery(id+"F0.wireOp",EDGE,"E2.3.3.0"),sQuery(id+"F0.wireOp",EDGE,"E2.3.4.0"),sQuery(id+"F0.wireOp",EDGE,"E2.3.5.0"),sQuery(id+"F0.wireOp",EDGE,"E2.4.0.0"),sQuery(id+"F0.wireOp",EDGE,"E2.4.1.0"),sQuery(id+"F0.wireOp",EDGE,"E2.4.2.0"),sQuery(id+"F0.wireOp",EDGE,"E2.4.3.0"),sQuery(id+"F0.wireOp",EDGE,"E2.4.4.0"),sQuery(id+"F0.wireOp",EDGE,"E2.4.5.0"),sQuery(id+"F0.wireOp",EDGE,"E3.filletArc"),sQuery(id+"F0.wireOp",EDGE,"E4.filletArc"),sQuery(id+"F0.wireOp",EDGE,"E5.filletArc"),sQuery(id+"F0.wireOp",EDGE,"E6.filletArc")])],"isStart":false})});}
            var Q4;
            {var subQ0=sQuery(id+"F0.wireOp",EDGE,"E0.rect.bottom");var subQ1=sQuery(id+"F0.wireOp",EDGE,"E0.rect.top");Q4=makeQuery(id+"F5.boolean.opBoolean","SPLIT",FACE,{"disambiguationData":[TD([makeQuery(id+"F3.boolean.opBoolean","COPY",FACE,{"derivedFrom":makeQuery(id+"F3.opExtrude","SWEPT_FACE",FACE,{"disambiguationData":[OSD([sQuery(id+"F1.wireOp",EDGE,"E13.3.0.0")])]})})])],"derivedFrom":makeQuery(id+"F2.opExtrude","CAP_FACE",FACE,{"disambiguationData":[OSD([subQ0,subQ1,sQuery(id+"F0.wireOp",EDGE,"E0.rect.left"),sQuery(id+"F0.wireOp",EDGE,"E0.rect.right"),sQuery(id+"F0.wireOp",EDGE,"E1"),sQuery(id+"F0.wireOp",EDGE,"E2.0.1.0"),sQuery(id+"F0.wireOp",EDGE,"E2.0.2.0"),sQuery(id+"F0.wireOp",EDGE,"E2.0.3.0"),sQuery(id+"F0.wireOp",EDGE,"E2.0.4.0"),sQuery(id+"F0.wireOp",EDGE,"E2.0.5.0"),sQuery(id+"F0.wireOp",EDGE,"E2.1.0.0"),sQuery(id+"F0.wireOp",EDGE,"E2.1.1.0"),sQuery(id+"F0.wireOp",EDGE,"E2.1.2.0"),sQuery(id+"F0.wireOp",EDGE,"E2.1.3.0"),sQuery(id+"F0.wireOp",EDGE,"E2.1.4.0"),sQuery(id+"F0.wireOp",EDGE,"E2.1.5.0"),sQuery(id+"F0.wireOp",EDGE,"E2.2.0.0"),sQuery(id+"F0.wireOp",EDGE,"E2.2.1.0"),sQuery(id+"F0.wireOp",EDGE,"E2.2.2.0"),sQuery(id+"F0.wireOp",EDGE,"E2.2.3.0"),sQuery(id+"F0.wireOp",EDGE,"E2.2.4.0"),sQuery(id+"F0.wireOp",EDGE,"E2.2.5.0"),sQuery(id+"F0.wireOp",EDGE,"E2.3.0.0"),sQuery(id+"F0.wireOp",EDGE,"E2.3.1.0"),sQuery(id+"F0.wireOp",EDGE,"E2.3.2.0"),sQuery(id+"F0.wireOp",EDGE,"E2.3.3.0"),sQuery(id+"F0.wireOp",EDGE,"E2.3.4.0"),sQuery(id+"F0.wireOp",EDGE,"E2.3.5.0"),sQuery(id+"F0.wireOp",EDGE,"E2.4.0.0"),sQuery(id+"F0.wireOp",EDGE,"E2.4.1.0"),sQuery(id+"F0.wireOp",EDGE,"E2.4.2.0"),sQuery(id+"F0.wireOp",EDGE,"E2.4.3.0"),sQuery(id+"F0.wireOp",EDGE,"E2.4.4.0"),sQuery(id+"F0.wireOp",EDGE,"E2.4.5.0"),sQuery(id+"F0.wireOp",EDGE,"E3.filletArc"),sQuery(id+"F0.wireOp",EDGE,"E4.filletArc"),sQuery(id+"F0.wireOp",EDGE,"E5.filletArc"),sQuery(id+"F0.wireOp",EDGE,"E6.filletArc")])],"isStart":false})});}
            var Q5;
            {var subQ0=sQuery(id+"F0.wireOp",EDGE,"E0.rect.bottom");var subQ1=sQuery(id+"F0.wireOp",EDGE,"E0.rect.top");var subQ2=sQuery(id+"F0.wireOp",EDGE,"E0.rect.left");var subQ3=sQuery(id+"F0.wireOp",EDGE,"E3.filletArc");var subQ4=sQuery(id+"F0.wireOp",EDGE,"E4.filletArc");Q5=makeQuery(id+"F5.boolean.opBoolean","SPLIT",FACE,{"disambiguationData":[TD([makeQuery(id+"F2.opExtrude","SWEPT_FACE",FACE,{"disambiguationData":[OSD([subQ2])]})])],"derivedFrom":makeQuery(id+"F2.opExtrude","CAP_FACE",FACE,{"disambiguationData":[OSD([subQ0,subQ1,subQ2,sQuery(id+"F0.wireOp",EDGE,"E0.rect.right"),sQuery(id+"F0.wireOp",EDGE,"E1"),sQuery(id+"F0.wireOp",EDGE,"E2.0.1.0"),sQuery(id+"F0.wireOp",EDGE,"E2.0.2.0"),sQuery(id+"F0.wireOp",EDGE,"E2.0.3.0"),sQuery(id+"F0.wireOp",EDGE,"E2.0.4.0"),sQuery(id+"F0.wireOp",EDGE,"E2.0.5.0"),sQuery(id+"F0.wireOp",EDGE,"E2.1.0.0"),sQuery(id+"F0.wireOp",EDGE,"E2.1.1.0"),sQuery(id+"F0.wireOp",EDGE,"E2.1.2.0"),sQuery(id+"F0.wireOp",EDGE,"E2.1.3.0"),sQuery(id+"F0.wireOp",EDGE,"E2.1.4.0"),sQuery(id+"F0.wireOp",EDGE,"E2.1.5.0"),sQuery(id+"F0.wireOp",EDGE,"E2.2.0.0"),sQuery(id+"F0.wireOp",EDGE,"E2.2.1.0"),sQuery(id+"F0.wireOp",EDGE,"E2.2.2.0"),sQuery(id+"F0.wireOp",EDGE,"E2.2.3.0"),sQuery(id+"F0.wireOp",EDGE,"E2.2.4.0"),sQuery(id+"F0.wireOp",EDGE,"E2.2.5.0"),sQuery(id+"F0.wireOp",EDGE,"E2.3.0.0"),sQuery(id+"F0.wireOp",EDGE,"E2.3.1.0"),sQuery(id+"F0.wireOp",EDGE,"E2.3.2.0"),sQuery(id+"F0.wireOp",EDGE,"E2.3.3.0"),sQuery(id+"F0.wireOp",EDGE,"E2.3.4.0"),sQuery(id+"F0.wireOp",EDGE,"E2.3.5.0"),sQuery(id+"F0.wireOp",EDGE,"E2.4.0.0"),sQuery(id+"F0.wireOp",EDGE,"E2.4.1.0"),sQuery(id+"F0.wireOp",EDGE,"E2.4.2.0"),sQuery(id+"F0.wireOp",EDGE,"E2.4.3.0"),sQuery(id+"F0.wireOp",EDGE,"E2.4.4.0"),sQuery(id+"F0.wireOp",EDGE,"E2.4.5.0"),subQ3,subQ4,sQuery(id+"F0.wireOp",EDGE,"E5.filletArc"),sQuery(id+"F0.wireOp",EDGE,"E6.filletArc")])],"isStart":false})});}
            fillet(context, id + "F9", {"entities" : qUnion([Q0, Q1, Q2, Q3, Q4, Q5]), "radius" : 0.5 * mm, "tangentPropagation" : true, "allowEdgeOverflow" : false});
        }
    });
